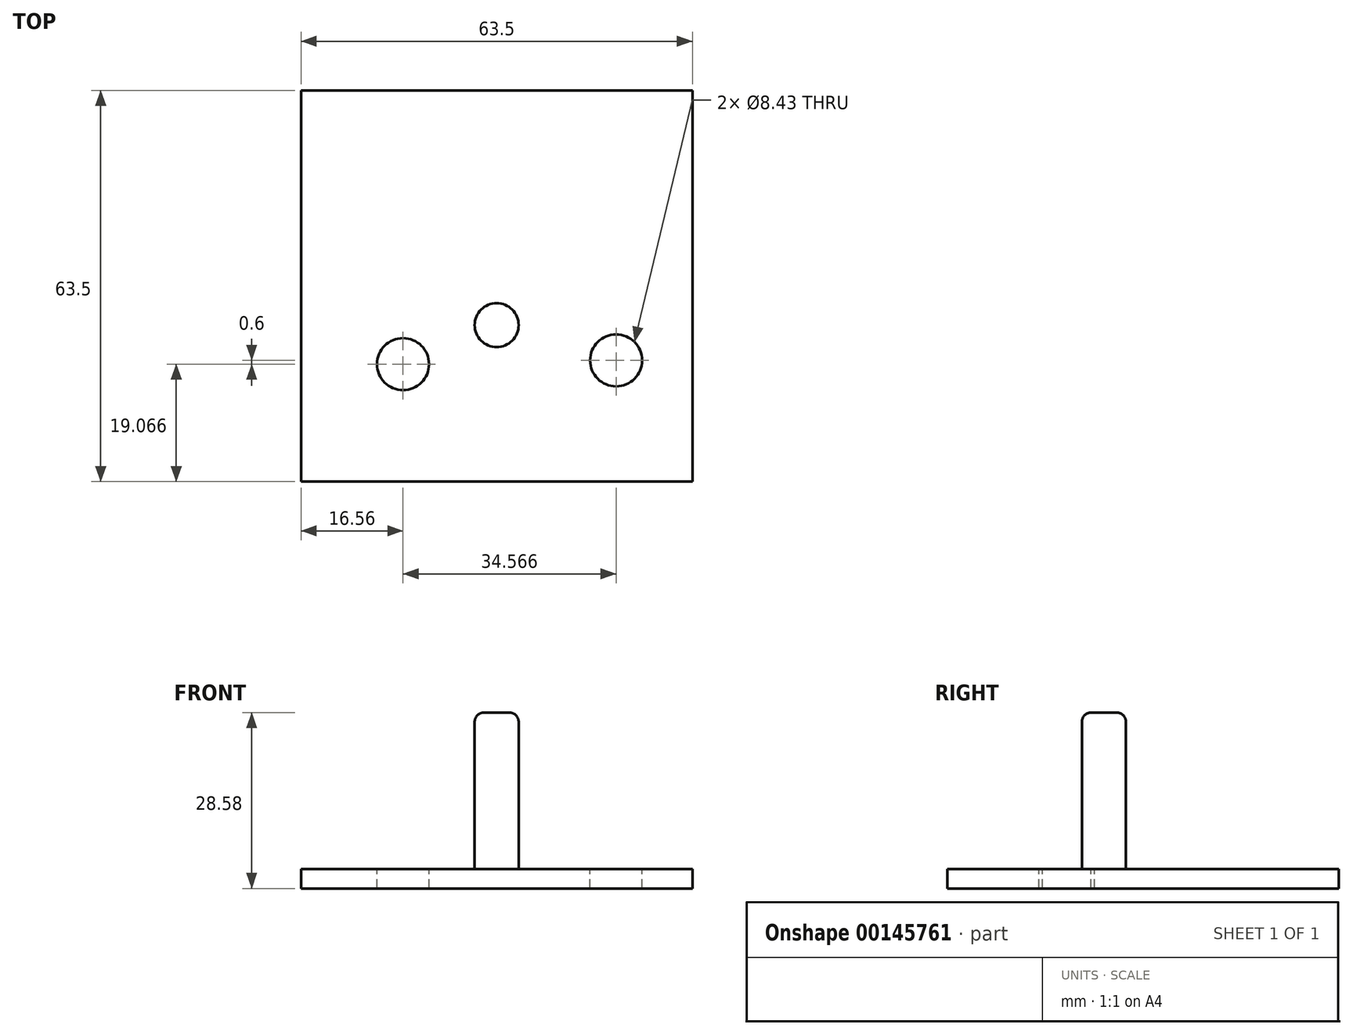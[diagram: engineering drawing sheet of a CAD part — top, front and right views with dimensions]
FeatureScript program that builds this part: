
annotation { "Feature Type Name" : "Feature", "Feature Type Description" : "" }
export const myFeature = defineFeature(function(context is Context, id is Id, definition is map)
    precondition{}
    {
        {
            var Q0;
            Q0=qCreatedBy(makeId("Top.planeOp"),FACE);
            var sketch = newSketch(context, id + "F0", { "sketchPlane" : qUnion([Q0])});
            skLineSegment(sketch, "E0.bottom", {"start": v(0, 0) * mm, "end": v(63.5, 0) * mm});
            skLineSegment(sketch, "E0.top", {"start": v(0, 63.5) * mm, "end": v(63.5, 63.5) * mm});
            skLineSegment(sketch, "E0.left", {"start": v(0, 0) * mm, "end": v(0, 63.5) * mm});
            skLineSegment(sketch, "E0.right", {"start": v(63.5, 0) * mm, "end": v(63.5, 63.5) * mm});
            skSolve(sketch);
        }
        {
            var Q0;
            Q0 = qSketchRegion(id + "F0", true);
            extrude(context, id + "F1", {"entities" : qUnion([Q0]), "depth" : 3.17 * mm});
        }
        {
            var Q0;
            Q0=makeQuery(id+"F1.opExtrude","CAP_FACE",FACE,{"disambiguationData":[OSD([sQuery(id+"F0.wireOp",EDGE,"E0.bottom"),sQuery(id+"F0.wireOp",EDGE,"E0.top"),sQuery(id+"F0.wireOp",EDGE,"E0.left"),sQuery(id+"F0.wireOp",EDGE,"E0.right")])],"isStart":false});
            var sketch = newSketch(context, id + "F2", { "sketchPlane" : qUnion([Q0])});
            skCircle(sketch, "E1", {"center": v(31.75, 25.4) * mm, "radius": 3.57 * mm});
            skLineSegment(sketch, "E2", {"start": v(31.75, 0) * mm, "end": v(31.75, 25.4) * mm});
            skSolve(sketch);
        }
        {
            var Q0;
            Q0 = qSketchRegion(id + "F2", true);
            extrude(context, id + "F3", {"entities" : qUnion([Q0]), "operationType" : NewBodyOperationType.ADD, "depth" : 25.4 * mm});
        }
        {
            var Q0;
            Q0=makeQuery(id+"F3.opExtrude","CAP_EDGE",EDGE,{"disambiguationData":[OSD([sQuery(id+"F2.wireOp",EDGE,"E1")])],"isStart":false});
            fillet(context, id + "F4", {"entities" : qUnion([Q0]), "radius" : 1.52 * mm, "tangentPropagation" : true, "allowEdgeOverflow" : false});
        }
        {
            var Q0;
            Q0=makeQuery(id+"F1.opExtrude","CAP_FACE",FACE,{"disambiguationData":[OSD([sQuery(id+"F0.wireOp",EDGE,"E0.bottom"),sQuery(id+"F0.wireOp",EDGE,"E0.top"),sQuery(id+"F0.wireOp",EDGE,"E0.left"),sQuery(id+"F0.wireOp",EDGE,"E0.right")])],"isStart":false});
            var sketch = newSketch(context, id + "F5", { "sketchPlane" : qUnion([Q0])});
            skPoint(sketch, "E3", {"position": v(16.56, 19.07) * mm});
            skPoint(sketch, "E4", {"position": v(51.13, 19.67) * mm});
            skLineSegment(sketch, "E5", {"start": v(-61.69, -9.33) * mm, "end": v(0, 13.45) * mm});
            skLineSegment(sketch, "E6", {"start": v(0, 13.45) * mm, "end": v(37.17, 39.5) * mm});
            skLineSegment(sketch, "E7", {"start": v(37.17, 39.5) * mm, "end": v(-43.06, -14.96) * mm});
            skLineSegment(sketch, "E8", {"start": v(-43.06, -14.96) * mm, "end": v(-40.2, -13.4) * mm});
            skSolve(sketch);
        }
        {
            var Q0;
            Q0=sQuery(id+"F5.wireOp",VERTEX,"E3");
            var Q1;
            Q1=sQuery(id+"F5.wireOp",VERTEX,"E4");
            var Q2;
            Q2=makeQuery(id+"F1.opExtrude","SWEPT_BODY",BODY,{"disambiguationData":[OSD([sQuery(id+"F0.wireOp",EDGE,"E0.bottom"),sQuery(id+"F0.wireOp",EDGE,"E0.top"),sQuery(id+"F0.wireOp",EDGE,"E0.left"),sQuery(id+"F0.wireOp",EDGE,"E0.right")])]});
            hole(context, id + "F6", {"style" : HoleStyle.SIMPLE, "endStyle" : HoleEndStyle.THROUGH, "standardTappedOrClearance" : lookupTablePath({ "standard" : "ANSI", "fit" : "Normal (ASME)", "size" : "5/16", "type" : "Clearance" }), "standardBlindInLast" : lookupTablePath({ "fit" : "Free", "standard" : "ANSI", "size" : "5/16", "type" : "Clearance" }), "holeDiameter" : 8.43 * mm, "locations" : qUnion([Q0, Q1]), "scope" : qUnion([Q2]), "isTappedThrough" : true});
        }
    });
